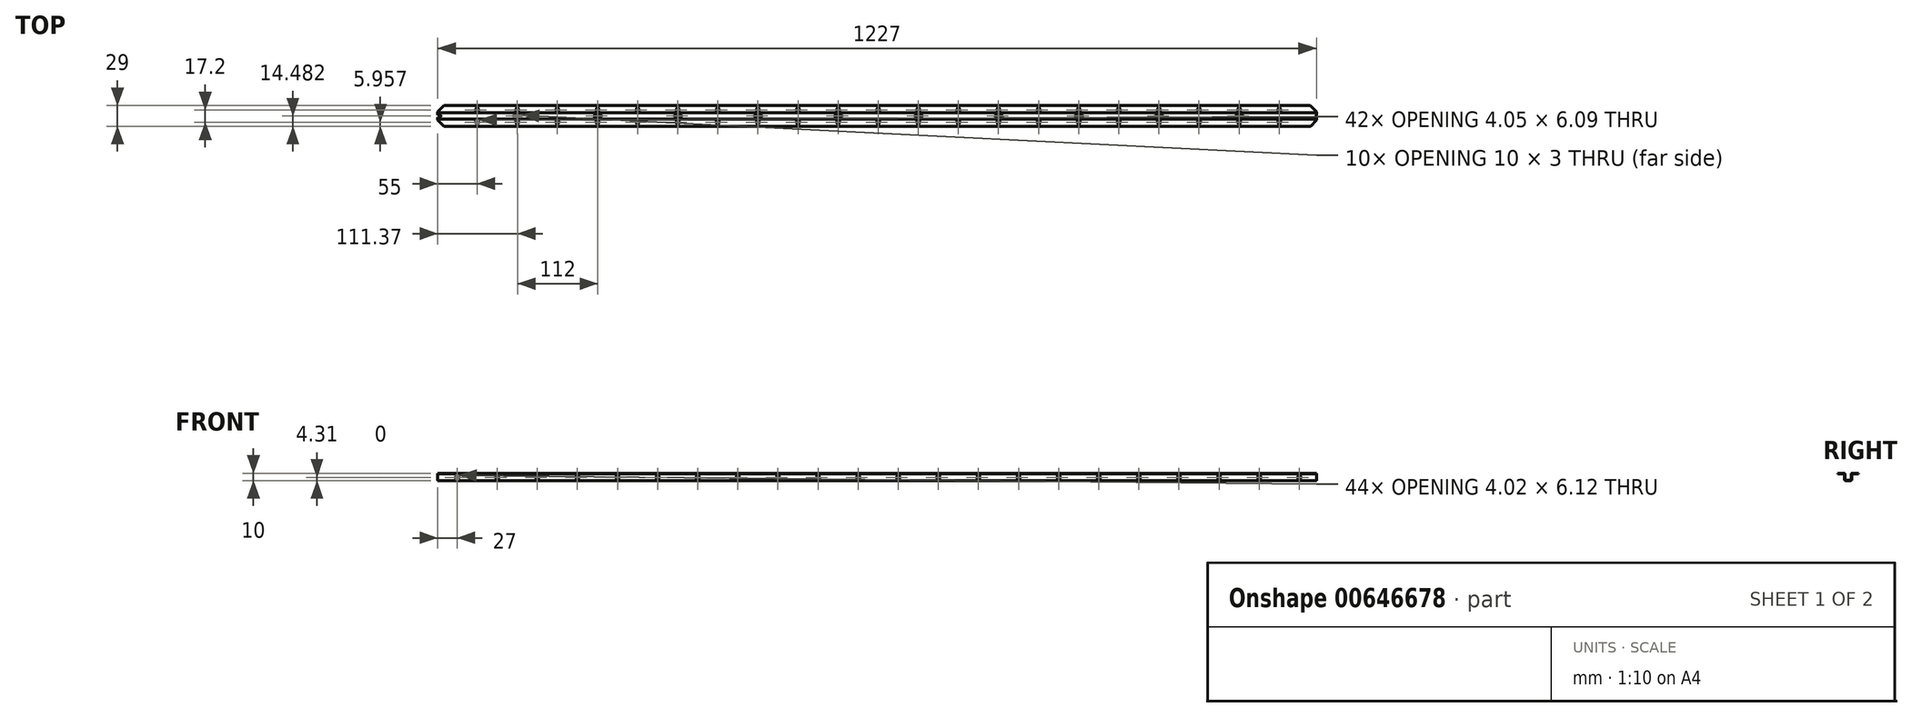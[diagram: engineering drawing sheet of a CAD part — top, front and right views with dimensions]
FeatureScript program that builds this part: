
annotation { "Feature Type Name" : "Feature", "Feature Type Description" : "" }
export const myFeature = defineFeature(function(context is Context, id is Id, definition is map)
    precondition{}
    {
        {
            var Q0;
            Q0=qCreatedBy(makeId("Right.planeOp"),FACE);
            var sketch = newSketch(context, id + "F0", { "sketchPlane" : qUnion([Q0])});
            skLineSegment(sketch, "E0", {"start": v(14.5, 5) * mm, "end": v(5.5, 5) * mm});
            skArc(sketch, "E1", {"start": v(5.5, 5) * mm, "mid": v(4.8, 4.7) * mm, "end": v(4.5, 4) * mm});
            skLineSegment(sketch, "E2", {"start": v(4.5, 4) * mm, "end": v(4.5, -4) * mm});
            skArc(sketch, "E3", {"start": v(4.5, -4) * mm, "mid": v(4.35, -4.35) * mm, "end": v(4, -4.5) * mm});
            skLineSegment(sketch, "E4", {"start": v(4, -4.5) * mm, "end": v(-4, -4.5) * mm});
            skArc(sketch, "E5", {"start": v(-4, -4.5) * mm, "mid": v(-4.35, -4.35) * mm, "end": v(-4.5, -4) * mm});
            skLineSegment(sketch, "E6", {"start": v(-4.5, -4) * mm, "end": v(-4.5, 4) * mm});
            skArc(sketch, "E7", {"start": v(-4.5, 4) * mm, "mid": v(-4.8, 4.7) * mm, "end": v(-5.5, 5) * mm});
            skLineSegment(sketch, "E8", {"start": v(-5.5, 5) * mm, "end": v(-14.5, 5) * mm});
            skLineSegment(sketch, "E9", {"start": v(-14.5, 5) * mm, "end": v(-14.5, 4.5) * mm});
            skLineSegment(sketch, "E10", {"start": v(-14.5, 4.5) * mm, "end": v(-5.5, 4.5) * mm});
            skArc(sketch, "E11", {"start": v(-5.5, 4.5) * mm, "mid": v(-5.15, 4.35) * mm, "end": v(-5, 4) * mm});
            skLineSegment(sketch, "E12", {"start": v(-5, 4) * mm, "end": v(-5, -4) * mm});
            skArc(sketch, "E13", {"start": v(-5, -4) * mm, "mid": v(-4.7, -4.7) * mm, "end": v(-4, -5) * mm});
            skLineSegment(sketch, "E14", {"start": v(-4, -5) * mm, "end": v(4, -5) * mm});
            skArc(sketch, "E15", {"start": v(4, -5) * mm, "mid": v(4.7, -4.7) * mm, "end": v(5, -4) * mm});
            skLineSegment(sketch, "E16", {"start": v(5, -4) * mm, "end": v(5, 4) * mm});
            skArc(sketch, "E17", {"start": v(5, 4) * mm, "mid": v(5.15, 4.35) * mm, "end": v(5.5, 4.5) * mm});
            skLineSegment(sketch, "E18", {"start": v(5.5, 4.5) * mm, "end": v(14.5, 4.5) * mm});
            skLineSegment(sketch, "E19", {"start": v(14.5, 4.5) * mm, "end": v(14.5, 5) * mm});
            skSolve(sketch);
        }
        {
            var Q0;
            Q0=qSketchRegion(id+"F0",true);
            extrude(context, id + "F1", {"entities" : qUnion([Q0]), "oppositeDirection" : true, "depth" : 1227 * mm, "offsetDistance" : 25 * mm});
        }
        {
            var Q0;
            Q0=makeQuery(id+"F1.opExtrude","SWEPT_FACE",FACE,{"disambiguationData":[OSD([sQuery(id+"F0.wireOp",EDGE,"E4")])]});
            var sketch = newSketch(context, id + "F2", { "sketchPlane" : qUnion([Q0])});
            skLineSegment(sketch, "E20.bottom", {"start": v(-1343.8, -1.5) * mm, "end": v(-1336.2, -1.5) * mm});
            skLineSegment(sketch, "E20.top", {"start": v(-1343.8, 1.5) * mm, "end": v(-1336.2, 1.5) * mm});
            skLineSegment(sketch, "E20.left", {"start": v(-1345, -0.3) * mm, "end": v(-1345, 0.3) * mm});
            skLineSegment(sketch, "E20.right", {"start": v(-1335, -0.3) * mm, "end": v(-1335, 0.3) * mm});
            skArc(sketch, "E21.filletArc", {"start": v(-1345, -0.3) * mm, "mid": v(-1344.65, -1.15) * mm, "end": v(-1343.8, -1.5) * mm});
            skArc(sketch, "E22.filletArc", {"start": v(-1343.8, 1.5) * mm, "mid": v(-1344.65, 1.15) * mm, "end": v(-1345, 0.3) * mm});
            skArc(sketch, "E23.filletArc", {"start": v(-1335, 0.3) * mm, "mid": v(-1335.35, 1.15) * mm, "end": v(-1336.2, 1.5) * mm});
            skArc(sketch, "E24.filletArc", {"start": v(-1336.2, -1.5) * mm, "mid": v(-1335.35, -1.15) * mm, "end": v(-1335, -0.3) * mm});
            skLineSegment(sketch, "E25.bottom", {"start": v(-1119.43, -1.52) * mm, "end": v(-1111.83, -1.52) * mm});
            skLineSegment(sketch, "E25.top", {"start": v(-1119.43, 1.48) * mm, "end": v(-1111.83, 1.48) * mm});
            skLineSegment(sketch, "E25.left", {"start": v(-1120.63, -0.32) * mm, "end": v(-1120.63, 0.28) * mm});
            skLineSegment(sketch, "E25.right", {"start": v(-1110.63, -0.32) * mm, "end": v(-1110.63, 0.28) * mm});
            skArc(sketch, "E26.filletArc", {"start": v(-1120.63, -0.32) * mm, "mid": v(-1120.28, -1.17) * mm, "end": v(-1119.43, -1.52) * mm});
            skArc(sketch, "E27.filletArc", {"start": v(-1119.43, 1.48) * mm, "mid": v(-1120.28, 1.13) * mm, "end": v(-1120.63, 0.28) * mm});
            skArc(sketch, "E28.filletArc", {"start": v(-1110.63, 0.28) * mm, "mid": v(-1110.98, 1.13) * mm, "end": v(-1111.83, 1.48) * mm});
            skArc(sketch, "E29.filletArc", {"start": v(-1111.83, -1.52) * mm, "mid": v(-1110.98, -1.17) * mm, "end": v(-1110.63, -0.32) * mm});
            skLineSegment(sketch, "E30.bottom", {"start": v(-1231.43, -1.52) * mm, "end": v(-1223.83, -1.52) * mm});
            skLineSegment(sketch, "E30.top", {"start": v(-1231.43, 1.48) * mm, "end": v(-1223.83, 1.48) * mm});
            skLineSegment(sketch, "E30.left", {"start": v(-1232.63, -0.32) * mm, "end": v(-1232.63, 0.28) * mm});
            skLineSegment(sketch, "E30.right", {"start": v(-1222.63, -0.32) * mm, "end": v(-1222.63, 0.28) * mm});
            skArc(sketch, "E31.filletArc", {"start": v(-1232.63, -0.32) * mm, "mid": v(-1232.28, -1.17) * mm, "end": v(-1231.43, -1.52) * mm});
            skArc(sketch, "E32.filletArc", {"start": v(-1231.43, 1.48) * mm, "mid": v(-1232.28, 1.13) * mm, "end": v(-1232.63, 0.28) * mm});
            skArc(sketch, "E33.filletArc", {"start": v(-1222.63, 0.28) * mm, "mid": v(-1222.98, 1.13) * mm, "end": v(-1223.83, 1.48) * mm});
            skArc(sketch, "E34.filletArc", {"start": v(-1223.83, -1.52) * mm, "mid": v(-1222.98, -1.17) * mm, "end": v(-1222.63, -0.32) * mm});
            skLineSegment(sketch, "E35.bottom", {"start": v(-1007.43, -1.52) * mm, "end": v(-999.83, -1.52) * mm});
            skLineSegment(sketch, "E35.top", {"start": v(-1007.43, 1.48) * mm, "end": v(-999.83, 1.48) * mm});
            skLineSegment(sketch, "E35.left", {"start": v(-1008.63, -0.32) * mm, "end": v(-1008.63, 0.28) * mm});
            skLineSegment(sketch, "E35.right", {"start": v(-998.63, -0.32) * mm, "end": v(-998.63, 0.28) * mm});
            skArc(sketch, "E36.filletArc", {"start": v(-1008.63, -0.32) * mm, "mid": v(-1008.28, -1.17) * mm, "end": v(-1007.43, -1.52) * mm});
            skArc(sketch, "E37.filletArc", {"start": v(-1007.43, 1.48) * mm, "mid": v(-1008.28, 1.13) * mm, "end": v(-1008.63, 0.28) * mm});
            skArc(sketch, "E38.filletArc", {"start": v(-998.63, 0.28) * mm, "mid": v(-998.98, 1.13) * mm, "end": v(-999.83, 1.48) * mm});
            skArc(sketch, "E39.filletArc", {"start": v(-999.83, -1.52) * mm, "mid": v(-998.98, -1.17) * mm, "end": v(-998.63, -0.32) * mm});
            skLineSegment(sketch, "E40.1.0.0", {"start": v(-895.43, -1.52) * mm, "end": v(-887.83, -1.52) * mm});
            skArc(sketch, "E40.1.0.1", {"start": v(-896.63, -0.32) * mm, "mid": v(-896.28, -1.17) * mm, "end": v(-895.43, -1.52) * mm});
            skLineSegment(sketch, "E40.1.0.2", {"start": v(-896.63, -0.32) * mm, "end": v(-896.63, 0.28) * mm});
            skArc(sketch, "E40.1.0.3", {"start": v(-895.43, 1.48) * mm, "mid": v(-896.28, 1.13) * mm, "end": v(-896.63, 0.28) * mm});
            skLineSegment(sketch, "E40.1.0.4", {"start": v(-895.43, 1.48) * mm, "end": v(-887.83, 1.48) * mm});
            skArc(sketch, "E40.1.0.5", {"start": v(-886.63, 0.28) * mm, "mid": v(-886.98, 1.13) * mm, "end": v(-887.83, 1.48) * mm});
            skLineSegment(sketch, "E40.1.0.6", {"start": v(-886.63, -0.32) * mm, "end": v(-886.63, 0.28) * mm});
            skArc(sketch, "E40.1.0.7", {"start": v(-887.83, -1.52) * mm, "mid": v(-886.98, -1.17) * mm, "end": v(-886.63, -0.32) * mm});
            skLineSegment(sketch, "E40.2.0.0", {"start": v(-783.43, -1.52) * mm, "end": v(-775.83, -1.52) * mm});
            skArc(sketch, "E40.2.0.1", {"start": v(-784.63, -0.32) * mm, "mid": v(-784.28, -1.17) * mm, "end": v(-783.43, -1.52) * mm});
            skLineSegment(sketch, "E40.2.0.2", {"start": v(-784.63, -0.32) * mm, "end": v(-784.63, 0.28) * mm});
            skArc(sketch, "E40.2.0.3", {"start": v(-783.43, 1.48) * mm, "mid": v(-784.28, 1.13) * mm, "end": v(-784.63, 0.28) * mm});
            skLineSegment(sketch, "E40.2.0.4", {"start": v(-783.43, 1.48) * mm, "end": v(-775.83, 1.48) * mm});
            skArc(sketch, "E40.2.0.5", {"start": v(-774.63, 0.28) * mm, "mid": v(-774.98, 1.13) * mm, "end": v(-775.83, 1.48) * mm});
            skLineSegment(sketch, "E40.2.0.6", {"start": v(-774.63, -0.32) * mm, "end": v(-774.63, 0.28) * mm});
            skArc(sketch, "E40.2.0.7", {"start": v(-775.83, -1.52) * mm, "mid": v(-774.98, -1.17) * mm, "end": v(-774.63, -0.32) * mm});
            skLineSegment(sketch, "E40.3.0.0", {"start": v(-671.43, -1.52) * mm, "end": v(-663.83, -1.52) * mm});
            skArc(sketch, "E40.3.0.1", {"start": v(-672.63, -0.32) * mm, "mid": v(-672.28, -1.17) * mm, "end": v(-671.43, -1.52) * mm});
            skLineSegment(sketch, "E40.3.0.2", {"start": v(-672.63, -0.32) * mm, "end": v(-672.63, 0.28) * mm});
            skArc(sketch, "E40.3.0.3", {"start": v(-671.43, 1.48) * mm, "mid": v(-672.28, 1.13) * mm, "end": v(-672.63, 0.28) * mm});
            skLineSegment(sketch, "E40.3.0.4", {"start": v(-671.43, 1.48) * mm, "end": v(-663.83, 1.48) * mm});
            skArc(sketch, "E40.3.0.5", {"start": v(-662.63, 0.28) * mm, "mid": v(-662.98, 1.13) * mm, "end": v(-663.83, 1.48) * mm});
            skLineSegment(sketch, "E40.3.0.6", {"start": v(-662.63, -0.32) * mm, "end": v(-662.63, 0.28) * mm});
            skArc(sketch, "E40.3.0.7", {"start": v(-663.83, -1.52) * mm, "mid": v(-662.98, -1.17) * mm, "end": v(-662.63, -0.32) * mm});
            skLineSegment(sketch, "E40.4.0.0", {"start": v(-559.43, -1.52) * mm, "end": v(-551.83, -1.52) * mm});
            skArc(sketch, "E40.4.0.1", {"start": v(-560.63, -0.32) * mm, "mid": v(-560.28, -1.17) * mm, "end": v(-559.43, -1.52) * mm});
            skLineSegment(sketch, "E40.4.0.2", {"start": v(-560.63, -0.32) * mm, "end": v(-560.63, 0.28) * mm});
            skArc(sketch, "E40.4.0.3", {"start": v(-559.43, 1.48) * mm, "mid": v(-560.28, 1.13) * mm, "end": v(-560.63, 0.28) * mm});
            skLineSegment(sketch, "E40.4.0.4", {"start": v(-559.43, 1.48) * mm, "end": v(-551.83, 1.48) * mm});
            skArc(sketch, "E40.4.0.5", {"start": v(-550.63, 0.28) * mm, "mid": v(-550.98, 1.13) * mm, "end": v(-551.83, 1.48) * mm});
            skLineSegment(sketch, "E40.4.0.6", {"start": v(-550.63, -0.32) * mm, "end": v(-550.63, 0.28) * mm});
            skArc(sketch, "E40.4.0.7", {"start": v(-551.83, -1.52) * mm, "mid": v(-550.98, -1.17) * mm, "end": v(-550.63, -0.32) * mm});
            skLineSegment(sketch, "E40.5.0.0", {"start": v(-447.43, -1.52) * mm, "end": v(-439.83, -1.52) * mm});
            skArc(sketch, "E40.5.0.1", {"start": v(-448.63, -0.32) * mm, "mid": v(-448.28, -1.17) * mm, "end": v(-447.43, -1.52) * mm});
            skLineSegment(sketch, "E40.5.0.2", {"start": v(-448.63, -0.32) * mm, "end": v(-448.63, 0.28) * mm});
            skArc(sketch, "E40.5.0.3", {"start": v(-447.43, 1.48) * mm, "mid": v(-448.28, 1.13) * mm, "end": v(-448.63, 0.28) * mm});
            skLineSegment(sketch, "E40.5.0.4", {"start": v(-447.43, 1.48) * mm, "end": v(-439.83, 1.48) * mm});
            skArc(sketch, "E40.5.0.5", {"start": v(-438.63, 0.28) * mm, "mid": v(-438.98, 1.13) * mm, "end": v(-439.83, 1.48) * mm});
            skLineSegment(sketch, "E40.5.0.6", {"start": v(-438.63, -0.32) * mm, "end": v(-438.63, 0.28) * mm});
            skArc(sketch, "E40.5.0.7", {"start": v(-439.83, -1.52) * mm, "mid": v(-438.98, -1.17) * mm, "end": v(-438.63, -0.32) * mm});
            skLineSegment(sketch, "E40.6.0.0", {"start": v(-335.43, -1.52) * mm, "end": v(-327.83, -1.52) * mm});
            skArc(sketch, "E40.6.0.1", {"start": v(-336.63, -0.32) * mm, "mid": v(-336.28, -1.17) * mm, "end": v(-335.43, -1.52) * mm});
            skLineSegment(sketch, "E40.6.0.2", {"start": v(-336.63, -0.32) * mm, "end": v(-336.63, 0.28) * mm});
            skArc(sketch, "E40.6.0.3", {"start": v(-335.43, 1.48) * mm, "mid": v(-336.28, 1.13) * mm, "end": v(-336.63, 0.28) * mm});
            skLineSegment(sketch, "E40.6.0.4", {"start": v(-335.43, 1.48) * mm, "end": v(-327.83, 1.48) * mm});
            skArc(sketch, "E40.6.0.5", {"start": v(-326.63, 0.28) * mm, "mid": v(-326.98, 1.13) * mm, "end": v(-327.83, 1.48) * mm});
            skLineSegment(sketch, "E40.6.0.6", {"start": v(-326.63, -0.32) * mm, "end": v(-326.63, 0.28) * mm});
            skArc(sketch, "E40.6.0.7", {"start": v(-327.83, -1.52) * mm, "mid": v(-326.98, -1.17) * mm, "end": v(-326.63, -0.32) * mm});
            skLineSegment(sketch, "E40.7.0.0", {"start": v(-223.43, -1.52) * mm, "end": v(-215.83, -1.52) * mm});
            skArc(sketch, "E40.7.0.1", {"start": v(-224.63, -0.32) * mm, "mid": v(-224.28, -1.17) * mm, "end": v(-223.43, -1.52) * mm});
            skLineSegment(sketch, "E40.7.0.2", {"start": v(-224.63, -0.32) * mm, "end": v(-224.63, 0.28) * mm});
            skArc(sketch, "E40.7.0.3", {"start": v(-223.43, 1.48) * mm, "mid": v(-224.28, 1.13) * mm, "end": v(-224.63, 0.28) * mm});
            skLineSegment(sketch, "E40.7.0.4", {"start": v(-223.43, 1.48) * mm, "end": v(-215.83, 1.48) * mm});
            skArc(sketch, "E40.7.0.5", {"start": v(-214.63, 0.28) * mm, "mid": v(-214.98, 1.13) * mm, "end": v(-215.83, 1.48) * mm});
            skLineSegment(sketch, "E40.7.0.6", {"start": v(-214.63, -0.32) * mm, "end": v(-214.63, 0.28) * mm});
            skArc(sketch, "E40.7.0.7", {"start": v(-215.83, -1.52) * mm, "mid": v(-214.98, -1.17) * mm, "end": v(-214.63, -0.32) * mm});
            skLineSegment(sketch, "E40.8.0.0", {"start": v(-111.43, -1.52) * mm, "end": v(-103.83, -1.52) * mm});
            skArc(sketch, "E40.8.0.1", {"start": v(-112.63, -0.32) * mm, "mid": v(-112.28, -1.17) * mm, "end": v(-111.43, -1.52) * mm});
            skLineSegment(sketch, "E40.8.0.2", {"start": v(-112.63, -0.32) * mm, "end": v(-112.63, 0.28) * mm});
            skArc(sketch, "E40.8.0.3", {"start": v(-111.43, 1.48) * mm, "mid": v(-112.28, 1.13) * mm, "end": v(-112.63, 0.28) * mm});
            skLineSegment(sketch, "E40.8.0.4", {"start": v(-111.43, 1.48) * mm, "end": v(-103.83, 1.48) * mm});
            skArc(sketch, "E40.8.0.5", {"start": v(-102.63, 0.28) * mm, "mid": v(-102.98, 1.13) * mm, "end": v(-103.83, 1.48) * mm});
            skLineSegment(sketch, "E40.8.0.6", {"start": v(-102.63, -0.32) * mm, "end": v(-102.63, 0.28) * mm});
            skArc(sketch, "E40.8.0.7", {"start": v(-103.83, -1.52) * mm, "mid": v(-102.98, -1.17) * mm, "end": v(-102.63, -0.32) * mm});
            skLineSegment(sketch, "E40.9.0.0", {"start": v(0.57, -1.52) * mm, "end": v(8.17, -1.52) * mm});
            skArc(sketch, "E40.9.0.1", {"start": v(-0.63, -0.32) * mm, "mid": v(-0.28, -1.17) * mm, "end": v(0.57, -1.52) * mm});
            skLineSegment(sketch, "E40.9.0.2", {"start": v(-0.63, -0.32) * mm, "end": v(-0.63, 0.28) * mm});
            skArc(sketch, "E40.9.0.3", {"start": v(0.57, 1.48) * mm, "mid": v(-0.28, 1.13) * mm, "end": v(-0.63, 0.28) * mm});
            skLineSegment(sketch, "E40.9.0.4", {"start": v(0.57, 1.48) * mm, "end": v(8.17, 1.48) * mm});
            skArc(sketch, "E40.9.0.5", {"start": v(9.37, 0.28) * mm, "mid": v(9.02, 1.13) * mm, "end": v(8.17, 1.48) * mm});
            skLineSegment(sketch, "E40.9.0.6", {"start": v(9.37, -0.32) * mm, "end": v(9.37, 0.28) * mm});
            skArc(sketch, "E40.9.0.7", {"start": v(8.17, -1.52) * mm, "mid": v(9.02, -1.17) * mm, "end": v(9.37, -0.32) * mm});
            skLineSegment(sketch, "E40.direction1", {"start": v(-998.63, -0.32) * mm, "end": v(-886.63, -0.32) * mm, "construction": true});
            skSolve(sketch);
        }
        {
            var Q0;
            Q0=qSketchRegion(id+"F2",true);
            extrude(context, id + "F3", {"entities" : qUnion([Q0]), "operationType" : NewBodyOperationType.REMOVE, "endBound" : BoundingType.THROUGH_ALL, "oppositeDirection" : true, "depth" : 25 * mm, "offsetDistance" : 25 * mm});
        }
        {
            var Q0;
            Q0=makeQuery(id+"F1.opExtrude","SWEPT_FACE",FACE,{"disambiguationData":[OSD([sQuery(id+"F0.wireOp",EDGE,"E12")])]});
            var sketch = newSketch(context, id + "F4", { "sketchPlane" : qUnion([Q0])});
            skEllipse(sketch, "E41", {"center": v(-1312, -0.69) * mm, "majorRadius": 3.06 * mm, "minorRadius": 2.01 * mm, "majorAxis": v(0, 1)});
            skEllipse(sketch, "E42.1.0.0", {"center": v(-1256, -0.69) * mm, "majorRadius": 3.06 * mm, "minorRadius": 2.01 * mm, "majorAxis": v(0, 1)});
            skEllipse(sketch, "E42.2.0.0", {"center": v(-1200, -0.69) * mm, "majorRadius": 3.06 * mm, "minorRadius": 2.01 * mm, "majorAxis": v(0, 1)});
            skEllipse(sketch, "E42.3.0.0", {"center": v(-1144, -0.69) * mm, "majorRadius": 3.06 * mm, "minorRadius": 2.01 * mm, "majorAxis": v(0, 1)});
            skEllipse(sketch, "E42.4.0.0", {"center": v(-1088, -0.69) * mm, "majorRadius": 3.06 * mm, "minorRadius": 2.01 * mm, "majorAxis": v(0, 1)});
            skEllipse(sketch, "E42.5.0.0", {"center": v(-1032, -0.69) * mm, "majorRadius": 3.06 * mm, "minorRadius": 2.01 * mm, "majorAxis": v(0, 1)});
            skEllipse(sketch, "E42.6.0.0", {"center": v(-976, -0.69) * mm, "majorRadius": 3.06 * mm, "minorRadius": 2.01 * mm, "majorAxis": v(0, 1)});
            skEllipse(sketch, "E42.7.0.0", {"center": v(-920, -0.69) * mm, "majorRadius": 3.06 * mm, "minorRadius": 2.01 * mm, "majorAxis": v(0, 1)});
            skEllipse(sketch, "E42.8.0.0", {"center": v(-864, -0.69) * mm, "majorRadius": 3.06 * mm, "minorRadius": 2.01 * mm, "majorAxis": v(0, 1)});
            skEllipse(sketch, "E42.9.0.0", {"center": v(-808, -0.69) * mm, "majorRadius": 3.06 * mm, "minorRadius": 2.01 * mm, "majorAxis": v(0, 1)});
            skEllipse(sketch, "E42.10.0.0", {"center": v(-752, -0.69) * mm, "majorRadius": 3.06 * mm, "minorRadius": 2.01 * mm, "majorAxis": v(0, 1)});
            skEllipse(sketch, "E42.11.0.0", {"center": v(-696, -0.69) * mm, "majorRadius": 3.06 * mm, "minorRadius": 2.01 * mm, "majorAxis": v(0, 1)});
            skEllipse(sketch, "E42.12.0.0", {"center": v(-640, -0.69) * mm, "majorRadius": 3.06 * mm, "minorRadius": 2.01 * mm, "majorAxis": v(0, 1)});
            skEllipse(sketch, "E42.13.0.0", {"center": v(-584, -0.69) * mm, "majorRadius": 3.06 * mm, "minorRadius": 2.01 * mm, "majorAxis": v(0, 1)});
            skEllipse(sketch, "E42.14.0.0", {"center": v(-528, -0.69) * mm, "majorRadius": 3.06 * mm, "minorRadius": 2.01 * mm, "majorAxis": v(0, 1)});
            skEllipse(sketch, "E42.15.0.0", {"center": v(-472, -0.69) * mm, "majorRadius": 3.06 * mm, "minorRadius": 2.01 * mm, "majorAxis": v(0, 1)});
            skEllipse(sketch, "E42.16.0.0", {"center": v(-416, -0.69) * mm, "majorRadius": 3.06 * mm, "minorRadius": 2.01 * mm, "majorAxis": v(0, 1)});
            skEllipse(sketch, "E42.17.0.0", {"center": v(-360, -0.69) * mm, "majorRadius": 3.06 * mm, "minorRadius": 2.01 * mm, "majorAxis": v(0, 1)});
            skEllipse(sketch, "E42.18.0.0", {"center": v(-304, -0.69) * mm, "majorRadius": 3.06 * mm, "minorRadius": 2.01 * mm, "majorAxis": v(0, 1)});
            skEllipse(sketch, "E42.19.0.0", {"center": v(-248, -0.69) * mm, "majorRadius": 3.06 * mm, "minorRadius": 2.01 * mm, "majorAxis": v(0, 1)});
            skEllipse(sketch, "E42.20.0.0", {"center": v(-192, -0.69) * mm, "majorRadius": 3.06 * mm, "minorRadius": 2.01 * mm, "majorAxis": v(0, 1)});
            skEllipse(sketch, "E42.21.0.0", {"center": v(-136, -0.69) * mm, "majorRadius": 3.06 * mm, "minorRadius": 2.01 * mm, "majorAxis": v(0, 1)});
            skEllipse(sketch, "E42.22.0.0", {"center": v(-80, -0.69) * mm, "majorRadius": 3.06 * mm, "minorRadius": 2.01 * mm, "majorAxis": v(0, 1)});
            skEllipse(sketch, "E42.23.0.0", {"center": v(-24, -0.69) * mm, "majorRadius": 3.06 * mm, "minorRadius": 2.01 * mm, "majorAxis": v(0, 1)});
            skLineSegment(sketch, "E42.direction1", {"start": v(-1340, -0.69) * mm, "end": v(-1284, -0.69) * mm, "construction": true});
            skSolve(sketch);
        }
        {
            var Q0;
            Q0=qSketchRegion(id+"F4",true);
            extrude(context, id + "F5", {"entities" : qUnion([Q0]), "operationType" : NewBodyOperationType.REMOVE, "oppositeDirection" : true, "depth" : 15 * mm, "offsetDistance" : 25 * mm});
        }
        {
            var Q0;
            Q0=makeQuery(id+"F1.opExtrude","SWEPT_FACE",FACE,{"disambiguationData":[OSD([sQuery(id+"F0.wireOp",EDGE,"E8")])]});
            var sketch = newSketch(context, id + "F6", { "sketchPlane" : qUnion([Q0])});
            skEllipse(sketch, "E43", {"center": v(-1340, -8.54) * mm, "majorRadius": 3.04 * mm, "minorRadius": 2.03 * mm, "majorAxis": v(0, -1)});
            skEllipse(sketch, "E44.0.1.0", {"center": v(-1340, 8.66) * mm, "majorRadius": 3.04 * mm, "minorRadius": 2.03 * mm, "majorAxis": v(0, -1)});
            skEllipse(sketch, "E44.1.0.0", {"center": v(-1284, -8.54) * mm, "majorRadius": 3.04 * mm, "minorRadius": 2.03 * mm, "majorAxis": v(0, -1)});
            skEllipse(sketch, "E44.1.1.0", {"center": v(-1284, 8.66) * mm, "majorRadius": 3.04 * mm, "minorRadius": 2.03 * mm, "majorAxis": v(0, -1)});
            skEllipse(sketch, "E44.2.0.0", {"center": v(-1228, -8.54) * mm, "majorRadius": 3.04 * mm, "minorRadius": 2.03 * mm, "majorAxis": v(0, -1)});
            skEllipse(sketch, "E44.2.1.0", {"center": v(-1228, 8.66) * mm, "majorRadius": 3.04 * mm, "minorRadius": 2.03 * mm, "majorAxis": v(0, -1)});
            skEllipse(sketch, "E44.3.0.0", {"center": v(-1172, -8.54) * mm, "majorRadius": 3.04 * mm, "minorRadius": 2.03 * mm, "majorAxis": v(0, -1)});
            skEllipse(sketch, "E44.3.1.0", {"center": v(-1172, 8.66) * mm, "majorRadius": 3.04 * mm, "minorRadius": 2.03 * mm, "majorAxis": v(0, -1)});
            skEllipse(sketch, "E44.4.0.0", {"center": v(-1116, -8.54) * mm, "majorRadius": 3.04 * mm, "minorRadius": 2.03 * mm, "majorAxis": v(0, -1)});
            skEllipse(sketch, "E44.4.1.0", {"center": v(-1116, 8.66) * mm, "majorRadius": 3.04 * mm, "minorRadius": 2.03 * mm, "majorAxis": v(0, -1)});
            skEllipse(sketch, "E44.5.0.0", {"center": v(-1060, -8.54) * mm, "majorRadius": 3.04 * mm, "minorRadius": 2.03 * mm, "majorAxis": v(0, -1)});
            skEllipse(sketch, "E44.5.1.0", {"center": v(-1060, 8.66) * mm, "majorRadius": 3.04 * mm, "minorRadius": 2.03 * mm, "majorAxis": v(0, -1)});
            skEllipse(sketch, "E44.6.0.0", {"center": v(-1004, -8.54) * mm, "majorRadius": 3.04 * mm, "minorRadius": 2.03 * mm, "majorAxis": v(0, -1)});
            skEllipse(sketch, "E44.6.1.0", {"center": v(-1004, 8.66) * mm, "majorRadius": 3.04 * mm, "minorRadius": 2.03 * mm, "majorAxis": v(0, -1)});
            skEllipse(sketch, "E44.7.0.0", {"center": v(-948, -8.54) * mm, "majorRadius": 3.04 * mm, "minorRadius": 2.03 * mm, "majorAxis": v(0, -1)});
            skEllipse(sketch, "E44.7.1.0", {"center": v(-948, 8.66) * mm, "majorRadius": 3.04 * mm, "minorRadius": 2.03 * mm, "majorAxis": v(0, -1)});
            skEllipse(sketch, "E44.8.0.0", {"center": v(-892, -8.54) * mm, "majorRadius": 3.04 * mm, "minorRadius": 2.03 * mm, "majorAxis": v(0, -1)});
            skEllipse(sketch, "E44.8.1.0", {"center": v(-892, 8.66) * mm, "majorRadius": 3.04 * mm, "minorRadius": 2.03 * mm, "majorAxis": v(0, -1)});
            skEllipse(sketch, "E44.9.0.0", {"center": v(-836, -8.54) * mm, "majorRadius": 3.04 * mm, "minorRadius": 2.03 * mm, "majorAxis": v(0, -1)});
            skEllipse(sketch, "E44.9.1.0", {"center": v(-836, 8.66) * mm, "majorRadius": 3.04 * mm, "minorRadius": 2.03 * mm, "majorAxis": v(0, -1)});
            skEllipse(sketch, "E44.10.0.0", {"center": v(-780, -8.54) * mm, "majorRadius": 3.04 * mm, "minorRadius": 2.03 * mm, "majorAxis": v(0, -1)});
            skEllipse(sketch, "E44.10.1.0", {"center": v(-780, 8.66) * mm, "majorRadius": 3.04 * mm, "minorRadius": 2.03 * mm, "majorAxis": v(0, -1)});
            skEllipse(sketch, "E44.11.0.0", {"center": v(-724, -8.54) * mm, "majorRadius": 3.04 * mm, "minorRadius": 2.03 * mm, "majorAxis": v(0, -1)});
            skEllipse(sketch, "E44.11.1.0", {"center": v(-724, 8.66) * mm, "majorRadius": 3.04 * mm, "minorRadius": 2.03 * mm, "majorAxis": v(0, -1)});
            skEllipse(sketch, "E44.12.0.0", {"center": v(-668, -8.54) * mm, "majorRadius": 3.04 * mm, "minorRadius": 2.03 * mm, "majorAxis": v(0, -1)});
            skEllipse(sketch, "E44.12.1.0", {"center": v(-668, 8.66) * mm, "majorRadius": 3.04 * mm, "minorRadius": 2.03 * mm, "majorAxis": v(0, -1)});
            skEllipse(sketch, "E44.13.0.0", {"center": v(-612, -8.54) * mm, "majorRadius": 3.04 * mm, "minorRadius": 2.03 * mm, "majorAxis": v(0, -1)});
            skEllipse(sketch, "E44.13.1.0", {"center": v(-612, 8.66) * mm, "majorRadius": 3.04 * mm, "minorRadius": 2.03 * mm, "majorAxis": v(0, -1)});
            skEllipse(sketch, "E44.14.0.0", {"center": v(-556, -8.54) * mm, "majorRadius": 3.04 * mm, "minorRadius": 2.03 * mm, "majorAxis": v(0, -1)});
            skEllipse(sketch, "E44.14.1.0", {"center": v(-556, 8.66) * mm, "majorRadius": 3.04 * mm, "minorRadius": 2.03 * mm, "majorAxis": v(0, -1)});
            skEllipse(sketch, "E44.15.0.0", {"center": v(-500, -8.54) * mm, "majorRadius": 3.04 * mm, "minorRadius": 2.03 * mm, "majorAxis": v(0, -1)});
            skEllipse(sketch, "E44.15.1.0", {"center": v(-500, 8.66) * mm, "majorRadius": 3.04 * mm, "minorRadius": 2.03 * mm, "majorAxis": v(0, -1)});
            skEllipse(sketch, "E44.16.0.0", {"center": v(-444, -8.54) * mm, "majorRadius": 3.04 * mm, "minorRadius": 2.03 * mm, "majorAxis": v(0, -1)});
            skEllipse(sketch, "E44.16.1.0", {"center": v(-444, 8.66) * mm, "majorRadius": 3.04 * mm, "minorRadius": 2.03 * mm, "majorAxis": v(0, -1)});
            skEllipse(sketch, "E44.17.0.0", {"center": v(-388, -8.54) * mm, "majorRadius": 3.04 * mm, "minorRadius": 2.03 * mm, "majorAxis": v(0, -1)});
            skEllipse(sketch, "E44.17.1.0", {"center": v(-388, 8.66) * mm, "majorRadius": 3.04 * mm, "minorRadius": 2.03 * mm, "majorAxis": v(0, -1)});
            skEllipse(sketch, "E44.18.0.0", {"center": v(-332, -8.54) * mm, "majorRadius": 3.04 * mm, "minorRadius": 2.03 * mm, "majorAxis": v(0, -1)});
            skEllipse(sketch, "E44.18.1.0", {"center": v(-332, 8.66) * mm, "majorRadius": 3.04 * mm, "minorRadius": 2.03 * mm, "majorAxis": v(0, -1)});
            skEllipse(sketch, "E44.19.0.0", {"center": v(-276, -8.54) * mm, "majorRadius": 3.04 * mm, "minorRadius": 2.03 * mm, "majorAxis": v(0, -1)});
            skEllipse(sketch, "E44.19.1.0", {"center": v(-276, 8.66) * mm, "majorRadius": 3.04 * mm, "minorRadius": 2.03 * mm, "majorAxis": v(0, -1)});
            skEllipse(sketch, "E44.20.0.0", {"center": v(-220, -8.54) * mm, "majorRadius": 3.04 * mm, "minorRadius": 2.03 * mm, "majorAxis": v(0, -1)});
            skEllipse(sketch, "E44.20.1.0", {"center": v(-220, 8.66) * mm, "majorRadius": 3.04 * mm, "minorRadius": 2.03 * mm, "majorAxis": v(0, -1)});
            skEllipse(sketch, "E44.21.0.0", {"center": v(-164, -8.54) * mm, "majorRadius": 3.04 * mm, "minorRadius": 2.03 * mm, "majorAxis": v(0, -1)});
            skEllipse(sketch, "E44.21.1.0", {"center": v(-164, 8.66) * mm, "majorRadius": 3.04 * mm, "minorRadius": 2.03 * mm, "majorAxis": v(0, -1)});
            skEllipse(sketch, "E44.22.0.0", {"center": v(-108, -8.54) * mm, "majorRadius": 3.04 * mm, "minorRadius": 2.03 * mm, "majorAxis": v(0, -1)});
            skEllipse(sketch, "E44.22.1.0", {"center": v(-108, 8.66) * mm, "majorRadius": 3.04 * mm, "minorRadius": 2.03 * mm, "majorAxis": v(0, -1)});
            skEllipse(sketch, "E44.23.0.0", {"center": v(-52, -8.54) * mm, "majorRadius": 3.04 * mm, "minorRadius": 2.03 * mm, "majorAxis": v(0, -1)});
            skEllipse(sketch, "E44.23.1.0", {"center": v(-52, 8.66) * mm, "majorRadius": 3.04 * mm, "minorRadius": 2.03 * mm, "majorAxis": v(0, -1)});
            skLineSegment(sketch, "E44.direction1", {"start": v(-1340, -8.54) * mm, "end": v(-1284, -8.54) * mm, "construction": true});
            skLineSegment(sketch, "E44.direction2", {"start": v(-1340, -8.54) * mm, "end": v(-1340, 8.66) * mm, "construction": true});
            skSolve(sketch);
        }
        {
            var Q0;
            Q0=qSketchRegion(id+"F6",true);
            extrude(context, id + "F7", {"entities" : qUnion([Q0]), "operationType" : NewBodyOperationType.REMOVE, "endBound" : BoundingType.THROUGH_ALL, "oppositeDirection" : true, "depth" : 25 * mm, "offsetDistance" : 25 * mm});
        }
        {
            var Q0;
            Q0=makeQuery(id+"F1.opExtrude","SWEPT_FACE",FACE,{"disambiguationData":[OSD([sQuery(id+"F0.wireOp",EDGE,"E0")])]});
            var sketch = newSketch(context, id + "F8", { "sketchPlane" : qUnion([Q0])});
            skLineSegment(sketch, "E45", {"start": v(0, 5.5) * mm, "end": v(-8.36, 14.5) * mm});
            skLineSegment(sketch, "E46", {"start": v(-1227, 5.5) * mm, "end": v(-1218.27, 14.5) * mm});
            skSolve(sketch);
        }
        {
            var Q0;
            {var subQ9=sQuery(id+"F8.wireOp",EDGE,"E46");Q0=makeQuery(id+"F8.imprint","IMPRINT",FACE,{"disambiguationData":[TD([[makeQuery(id+"F8.imprint","IMPRINT",EDGE,{"derivedFrom":subQ9}),1.0]])]});}
            var Q1;
            {var subQ0=sQuery(id+"F8.wireOp",EDGE,"E45");Q1=makeQuery(id+"F8.imprint","IMPRINT",FACE,{"disambiguationData":[TD([[makeQuery(id+"F8.imprint","IMPRINT",EDGE,{"derivedFrom":subQ0}),-1.0]])]});}
            extrude(context, id + "F9", {"entities" : qUnion([Q0, Q1]), "operationType" : NewBodyOperationType.REMOVE, "endBound" : BoundingType.THROUGH_ALL, "oppositeDirection" : true, "depth" : 25 * mm, "offsetDistance" : 25 * mm});
        }
        {
            var Q0;
            Q0=makeQuery(id+"F1.opExtrude","SWEPT_FACE",FACE,{"disambiguationData":[OSD([sQuery(id+"F0.wireOp",EDGE,"E8")])]});
            var sketch = newSketch(context, id + "F10", { "sketchPlane" : qUnion([Q0])});
            skLineSegment(sketch, "E47", {"start": v(0, -5.5) * mm, "end": v(-8.31, -14.5) * mm});
            skLineSegment(sketch, "E48", {"start": v(-1227, -5.5) * mm, "end": v(-1218.5, -14.5) * mm});
            skSolve(sketch);
        }
        {
            var Q0;
            {var subQ10=sQuery(id+"F10.wireOp",EDGE,"E48");Q0=makeQuery(id+"F10.imprint","IMPRINT",FACE,{"disambiguationData":[TD([[makeQuery(id+"F10.imprint","IMPRINT",EDGE,{"derivedFrom":subQ10}),-1.0]])]});}
            var Q1;
            {var subQ0=sQuery(id+"F10.wireOp",EDGE,"E47");Q1=makeQuery(id+"F10.imprint","IMPRINT",FACE,{"disambiguationData":[TD([[makeQuery(id+"F10.imprint","IMPRINT",EDGE,{"derivedFrom":subQ0}),1.0]])]});}
            extrude(context, id + "F11", {"entities" : qUnion([Q0, Q1]), "operationType" : NewBodyOperationType.REMOVE, "endBound" : BoundingType.THROUGH_ALL, "oppositeDirection" : true, "depth" : 25 * mm, "offsetDistance" : 25 * mm});
        }
    });
